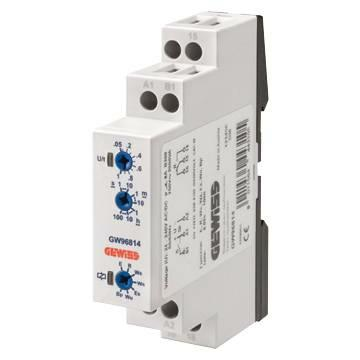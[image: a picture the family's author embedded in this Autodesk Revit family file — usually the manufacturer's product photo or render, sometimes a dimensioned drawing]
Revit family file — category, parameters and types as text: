
# Revit family: Power-ModularDevices-GEWISS-90AM-TIMER
name_source: partatom
category: Apparecchi elettrici
revit_build: Autodesk Revit 2016 (Build: 20161004_0715(x64)
units: mm (PartAtom-declared; Revit-internal decimal feet)

## family parameters
Condiviso = No
Host = Superficie
Mantenere orientamento annotazione = Sì
Numero OmniClass = 23.80.50.00
Punto di calcolo locali = Sì
Quota connettore circolare = Usa diametro
Taglio con vuoti quando caricato = No
Tipo di parte = Normale
Titolo OmniClass = Terminals for Power Supply

## types (3) — shared parameters
IDF = 10748350-1a66-4b6d-9d19-cdfde2de801f
IDT = bd5a74f1-e94d-4260-9f48-b7ba93ba89da
Immagine tipo = GW96815.jpg
Numero di poli = 1
Prospetto di default = 1219 mm
Spostamento_x = -3300 mm  [stored -10.8268 ft]
TIPO = GENERICO - 90AM TEMPORIZZATORI : GW96815 Temporizzatore a ciclo asimmetrico - 12…240Vac/dc - 1M
Technical sheet = https://www.gewiss.com
URL = https://www.gewiss.com
Version file RFA = 18.0
carico = Altro
potenza in watt = 0 V
zero-valued in all types: Barra_DIN

## per-type parameters (varying)
| type | Catalogue | Catalogue Range | Descrizione | EAN code | Electrocod | Modello | No. Chorus modules | No. of modules EN 50022 | Produttore | Rated coil voltage (V) | Regulation field | Regulation field: | SEO | Type | Type: |
| GW96809 Temporizzatore luce scale - 230Vac - 1M |  |  | TEMPORIZZATORE LUCE SCALE |  |  | GW96809 |  |  | GEWISS |  |  |  |  |  |  |
| GW96815 - ASYMMETRICAL TIMER | POWER | 90 AM | ASYMMETRICAL TIMER | 8011564760028 | 140 | GW96815 | 1 | 1 | GEWISS S.p.A. | 12....240 ac/dc | 0.05 s - 100 h | 0.05 s - 100 h | Timer | Asymmetric cycle | Asymmetric cycle |
| GW96814 - MULTIFUNCTIONAL TIMER | POWER | 90 AM | MULTIFUNCTIONAL TIMER | 8011564443105 | 140 | GW96814 | 1 | 1 | GEWISS S.p.A. | 24....240 ac/dc | 0.05 s - 100 h | 0.05 s - 100 h | Timer | Multi-function | Multi-function |

note: [stored X ft] marks values corroborated as IEEE doubles in the binary element streams (Revit-internal decimal feet)
